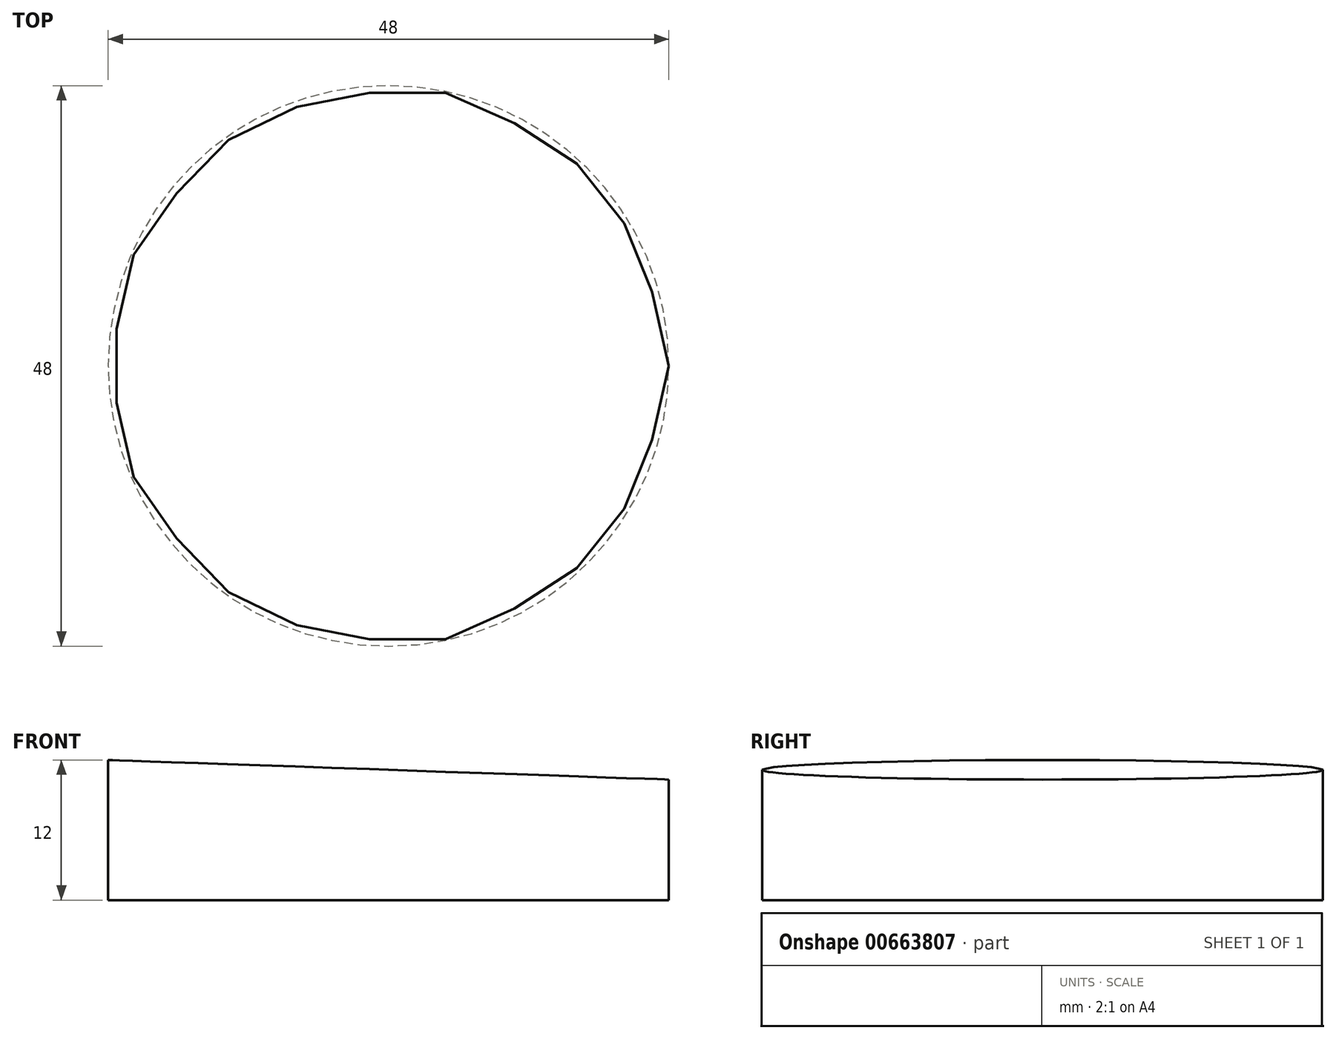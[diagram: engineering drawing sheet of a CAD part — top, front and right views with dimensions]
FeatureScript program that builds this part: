
annotation { "Feature Type Name" : "Feature", "Feature Type Description" : "" }
export const myFeature = defineFeature(function(context is Context, id is Id, definition is map)
    precondition{}
    {
        {
            var Q0;
            Q0=qCreatedBy(makeId("Top.planeOp"),FACE);
            var sketch = newSketch(context, id + "F0", { "sketchPlane" : qUnion([Q0])});
            skCircle(sketch, "E0", {"center": v(0, 0) * mm, "radius": 24 * mm});
            skSolve(sketch);
        }
        {
            var Q0;
            Q0=makeQuery(id+"F0.imprint","IMPRINT",FACE,{"disambiguationData":[TD([[makeQuery(id+"F0.imprint","IMPRINT",EDGE,{"derivedFrom":sQuery(id+"F0.wireOp",EDGE,"E0")}),1.0]])]});
            extrude(context, id + "F1", {"entities" : qUnion([Q0]), "depth" : 12 * mm, "offsetDistance" : 25 * mm});
        }
        {
            var Q0;
            Q0=qCreatedBy(makeId("Front.planeOp"),FACE);
            var sketch = newSketch(context, id + "F2", { "sketchPlane" : qUnion([Q0])});
            skLineSegment(sketch, "E1", {"start": v(-24.08, 12) * mm, "end": v(31.82, 10.05) * mm});
            skLineSegment(sketch, "E2", {"start": v(-24.08, 12) * mm, "end": v(-24.08, 19.97) * mm});
            skLineSegment(sketch, "E3", {"start": v(-24.08, 19.97) * mm, "end": v(21.2, 19.97) * mm});
            skLineSegment(sketch, "E4", {"start": v(21.2, 19.97) * mm, "end": v(38.38, 17.73) * mm});
            skLineSegment(sketch, "E5", {"start": v(38.38, 17.73) * mm, "end": v(31.82, 10.05) * mm});
            skSolve(sketch);
        }
        {
            var Q0;
            Q0 = qSketchRegion(id + "F2", true);
            extrude(context, id + "F3", {"entities" : qUnion([Q0]), "operationType" : NewBodyOperationType.REMOVE, "endBound" : BoundingType.SYMMETRIC, "depth" : 600 * mm, "offsetDistance" : 25 * mm});
        }
    });
